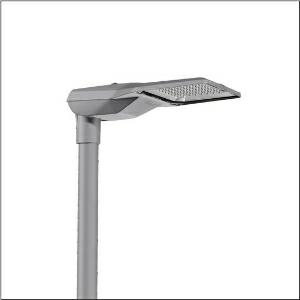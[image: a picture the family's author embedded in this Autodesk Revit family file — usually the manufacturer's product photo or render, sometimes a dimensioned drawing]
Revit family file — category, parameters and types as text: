
# Revit family: streetlight_sl_21_iq_midi___p0_8ab_5xe3r31v08nb_094b
name_source: partatom
category: Lighting Fixtures
units: mm (PartAtom-declared; Revit-internal decimal feet)

## family parameters
Cut with Voids When Loaded = No
Host = Face
Light Source = No
Part Type = Normal
Room Calculation Point = No
Round Connector Dimension = Use Diameter
Shared = No

## types (1)
- --- (1 x LED, 18710 lm, 136.6 W, 3000K)
    Apparent Load = 137 VA
    CIE Flux Codes = 39 72 97 100 100
    Color Rendering = 70
    Color Temperature = 3000K
    Default Elevation = 1800 mm
    Description = Streetlight SL 21 iQ midi, mast luminaire, primary light control with lens, of PMMA, primary optical cover: cover, of toughened safety glass, transparent, light distribution: P0.8aB, light emission: direct distribution, primary light characteristic: asymmetric, installation type: post-top, side-entry, LED, High Power LED, rated luminous flux: 18.710lm, luminous efficacy: 137lm/W, light colour: 730, colour temperature: 3000K, control gear: iQ-Street Remote, D4i with power reduction, control: pre-setting: logarithmic dimming characteristic, Street-Remote, Auto-Match, Temp-Guard, Lumen-Switch, Night-Set, Smart-Wire, Light-Fading, Desk-Remote (wireless, voltage-free reading and setting of iQ features in the workshop via application-optimized NFC function/RFID function), optimised constant luminous flux control (CLO 2.0), mains connection: 230..240V, AC, 50/60Hz, start of lifetime: 137W, end of service life: 144W, reduction: 61W, luminaire housing, of diecast aluminium, powder-coated, SITECO metallic grey (DB 702S), corrosivity category C5 high according to DIN EN ISO 12944, please order mast flange separately, inclination adjustable: 0°, 5°, 10°, 15°, sealing non-destructively replaceable, multi-level sealing system, length: 644mm, width: 335mm, height: 110mm, mast flange for spigot size: 42mm (side-entry): 5XC10008XM4, 60/48mm (side-entry/post-top): 5XC10108XM2, 76/60mm (side-entry/post-top): 5XC10108XM1, mounting height: 4..8m, Smart Interface above, protection rating (complete): IP66, insulation class (complete): insulation class II (safety insulation), certification: CE, ENEC, ENEC+, VDE, impact resistance: IK10, permissible operating ambient temperature for outdoor applications: -40..+50°C, standard-compliant lighting for roads and squares, packaging unit: 1 piece

Light Distribution: P0.8aB
    Height = 111 mm
    Lamp = 1 x LED
    Lamp Light Flux = 18710 lm
    Lamp Power = 136.6 W
    Lamp count = 1
    Length = 644 mm
    Luminous efficacy = 137 lm/W
    Manufacturer = Siteco
    ModVariant = No
    Model = 5XE3R31V08NB
    Number of Poles = 1
    OnlyDefault = Yes
    Power Factor = 1
    Product Name = Streetlight SL 21 iQ midi | P0.8aB
    Product group = mast luminaire | pylon top
    ProductGroupID = 6100
    Protection Class = Protection class II
    Protection Degree = IP 66
    RLX_Detail_Level = 1
    RLX_Emergency_Light_Flux = 0 lm
    RLX_Emergency_Type = 0
    RLX_Emergency_Type_DB = No
    RlxData = <blob elided: 90661 chars, md5=6cd06a85>
    Socket = socket
    Standby Power = 0 W
    System Light Flux = 18710 lm
    System Power = 137 W
    Type Comments = factory setting: luminous flux: 100 % | dim-lin: 254 | 733 mA
    Type Image = l_1004302.jpg
    URL = http://relux.com
    VarID = @adj_078953
    Voltage = 0 V
    Weight = 0.00 kg
    Width = 336 mm

## geometry (parser evidence)
native form markers: Blend x4, Sweep x11
no freeform markers — native parametric forms only
